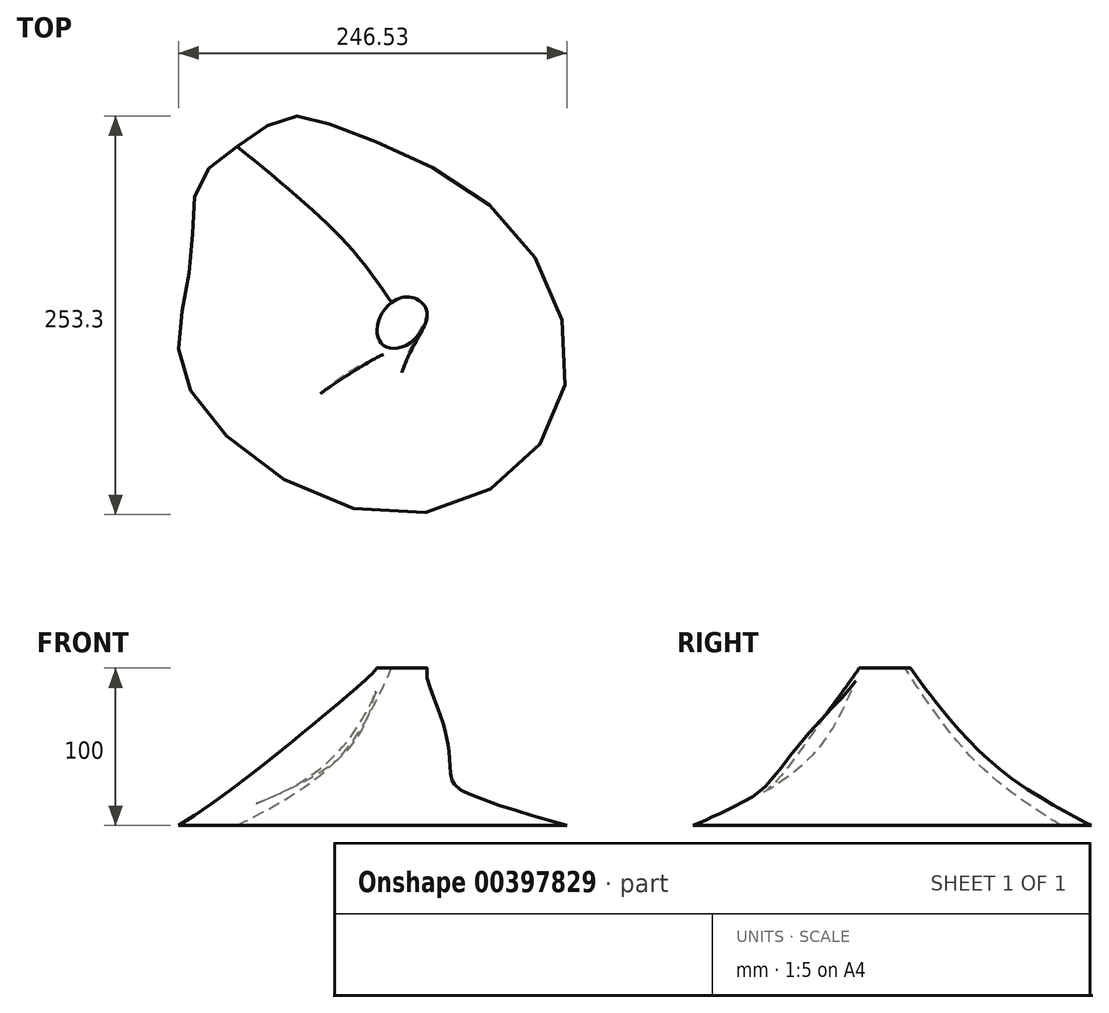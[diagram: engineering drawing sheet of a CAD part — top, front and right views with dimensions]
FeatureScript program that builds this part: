
annotation { "Feature Type Name" : "Feature", "Feature Type Description" : "" }
export const myFeature = defineFeature(function(context is Context, id is Id, definition is map)
    precondition{}
    {
        {
            var Q0;
            Q0=qCreatedBy(makeId("Top.planeOp"),FACE);
            var sketch = newSketch(context, id + "F0", { "sketchPlane" : qUnion([Q0])});
            skFitSpline(sketch, "E0", {"points": [v(-98.73, 105.18) * mm, v(-123.5, 81.06) * mm, v(-127.18, 39.33) * mm, v(-134.66, -5.28) * mm, v(-124.36, -56.37) * mm, v(0, -128.7) * mm, v(105.59, -61.77) * mm, v(72.2, 58.16) * mm, v(-31.91, 116.31) * mm, v(-66.53, 123.91) * mm, v(-98.73, 105.18) * mm]});
            skSolve(sketch);
        }
        {
            var Q0;
            Q0=qCreatedBy(makeId("Top.planeOp"),FACE);
            cPlane(context, id + "F1", {"entities" : qUnion([Q0]), "cplaneType" : CPlaneType.OFFSET, "offset" : 50 * mm, "width" : 152.4 * mm, "height" : 152.4 * mm});
        }
        {
            var Q0;
            Q0=qCreatedBy(makeId("Top.planeOp"),FACE);
            cPlane(context, id + "F2", {"entities" : qUnion([Q0]), "cplaneType" : CPlaneType.OFFSET, "offset" : 100 * mm, "width" : 152.4 * mm, "height" : 152.4 * mm});
        }
        {
            var Q0;
            Q0=qCreatedBy(id+"F1.planeOp",FACE);
            var sketch = newSketch(context, id + "F3", { "sketchPlane" : qUnion([Q0])});
            skFitSpline(sketch, "E1", {"points": [v(-27.73, 8.58) * mm, v(-60.42, 0) * mm, v(-58.77, -58.44) * mm, v(-35.4, -48.15) * mm, v(0, -62.36) * mm, v(11.56, -31.59) * mm, v(35.5, 21.5) * mm, v(0, 50.16) * mm, v(-31.33, 35.27) * mm, v(-27.73, 8.58) * mm]});
            skSolve(sketch);
        }
        {
            var Q0;
            Q0=qCreatedBy(id+"F2.planeOp",FACE);
            var sketch = newSketch(context, id + "F4", { "sketchPlane" : qUnion([Q0])});
            skFitSpline(sketch, "E2", {"points": [v(-8.68, -5.13) * mm, v(-6.25, -20.72) * mm, v(9.41, -20.75) * mm, v(21.98, 0) * mm, v(8.24, 9.5) * mm, v(-8.68, -5.13) * mm]});
            skSolve(sketch);
        }
        {
            var Q0;
            Q0=makeQuery(id+"F0.imprint","IMPRINT",FACE,{"disambiguationData":[TD([[makeQuery(id+"F0.imprint","IMPRINT",EDGE,{"derivedFrom":sQuery(id+"F0.wireOp",EDGE,"E0")}),1.0]])]});
            var Q1;
            Q1=makeQuery(id+"F3.imprint","IMPRINT",FACE,{"disambiguationData":[TD([[makeQuery(id+"F3.imprint","IMPRINT",EDGE,{"derivedFrom":sQuery(id+"F3.wireOp",EDGE,"E1")}),1.0]])]});
            var Q2;
            Q2=makeQuery(id+"F4.imprint","IMPRINT",FACE,{"disambiguationData":[TD([[makeQuery(id+"F4.imprint","IMPRINT",EDGE,{"derivedFrom":sQuery(id+"F4.wireOp",EDGE,"E2")}),1.0]])]});
            loft(context, id + "F5", {"sheetProfilesArray" : [{ "sheetProfileEntities" : qUnion([Q0]) }, { "sheetProfileEntities" : qUnion([Q1]) }, { "sheetProfileEntities" : qUnion([Q2]) }]});
        }
    });
